# Revit family: ITK_by ZPAS_Ввод щеточный кабельный верхний
name_source: partatom
category: Обобщенные модели
units: mm (PartAtom-declared; Revit-internal decimal feet)

## family parameters
Всегда вертикально = Да
Может служить основой для арматурных стержней = Нет
На основе рабочей плоскости = Нет
Общий = Нет
При загрузке вырезать с полостями = Нет
Размер круглого соединителя = Использовать диаметр
Тип детали = Нормальный
Точка расчета площади = Нет

## types (2) — shared parameters
ADSK_URL страницы изделия = https://www.itk-group.ru
ADSK_Версия Revit = 2019
ADSK_Версия семейства = 1.0
ADSK_Группирование = I. ЩИТЫ И ПУЛЬТЫ
ADSK_Единица измерения = шт
ADSK_Завод-изготовитель = IEK
ADSK_Марка = by ZPAS
ADSK_Материал наименование = Пластик
IEK_URL = https://www.itk-group.ru
IEK_Описание = Предотвращают попадание пыли в шкаф и на оборудование при заведении кабельных линий.
Удобны в монтаже и эксплуатации.
Соответствие российским и международным стандартам.
KSI_CMa_Строительные материалы = 01.7.14.03
KSI_CPr_Строительные изделия = 61.1.04.08
URL = https://www.iek.ru
Глубина = 20 мм
Изготовитель = ITK
Материал = Окраска - RAL 9005
Ширина = 100 мм

## per-type parameters (varying)
| type | ADSK_Код изделия | ADSK_Масса | ADSK_Наименование | IEK_Цена за единицу | Высота |
| В1000 | ZP-BE-1000 | 0.2 | ITK by ZPAS Ввод щеточный кабельный верхний 1000 | 3688.88 | 1000 мм |
| В1200 | ZP-BE-1200 | 0.3 | ITK by ZPAS Ввод щеточный кабельный верхний 1200 | 4399.15 | 1200 мм |
